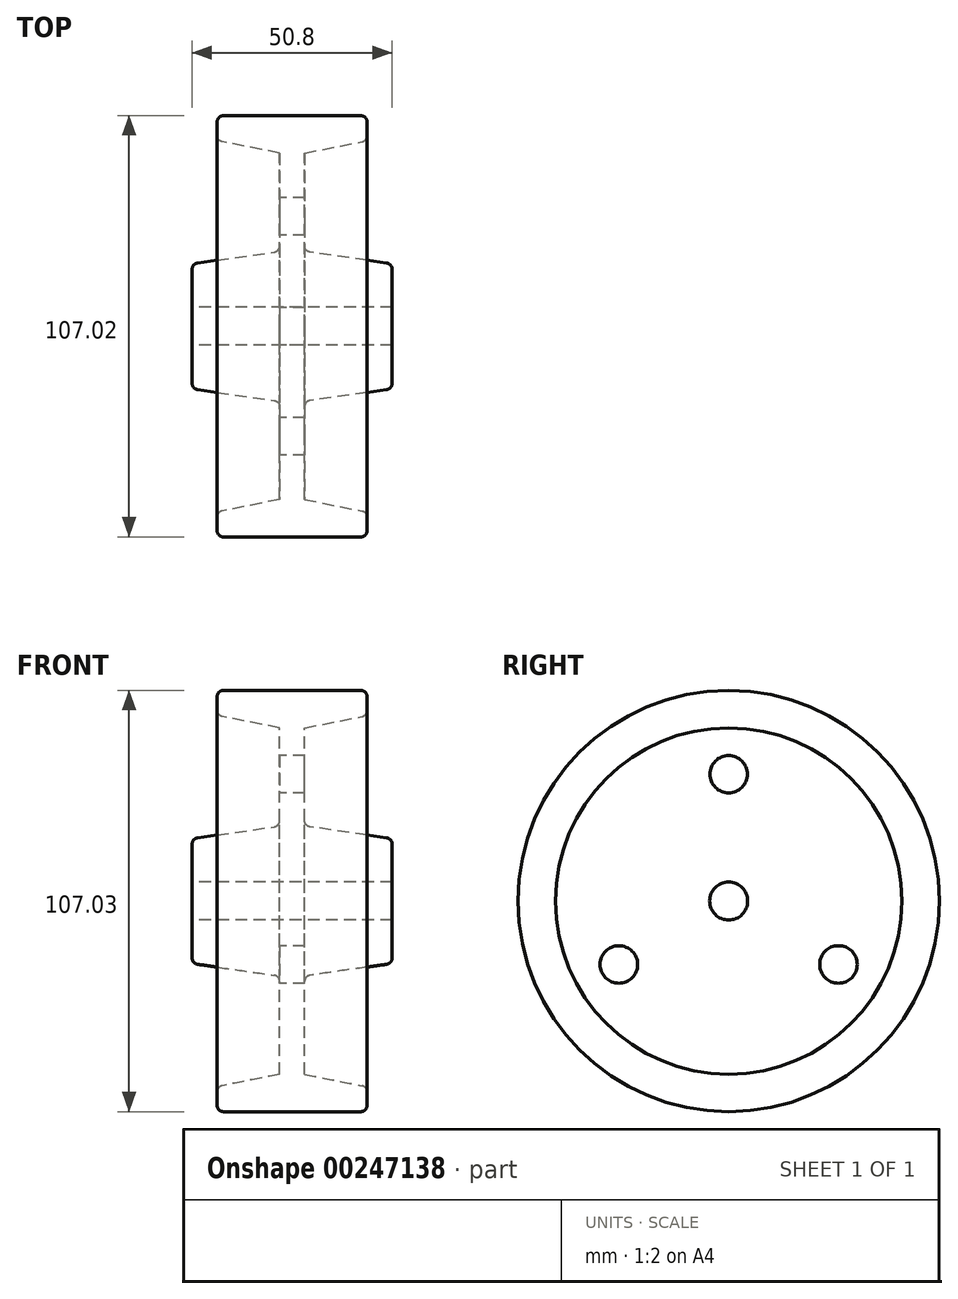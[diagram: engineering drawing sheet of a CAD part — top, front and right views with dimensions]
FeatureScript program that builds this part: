
annotation { "Feature Type Name" : "Feature", "Feature Type Description" : "" }
export const myFeature = defineFeature(function(context is Context, id is Id, definition is map)
    precondition{}
    {
        {
            var Q0;
            Q0=qCreatedBy(makeId("Front.planeOp"),FACE);
            var sketch = newSketch(context, id + "F0", { "sketchPlane" : qUnion([Q0])});
            skLineSegment(sketch, "E0", {"start": v(-20.15, 37.64) * mm, "end": v(14.77, 37.64) * mm});
            skLineSegment(sketch, "E1", {"start": v(-21.74, 36.05) * mm, "end": v(-21.74, 32.59) * mm});
            skLineSegment(sketch, "E2", {"start": v(16.36, 36.05) * mm, "end": v(16.36, 32.59) * mm});
            skLineSegment(sketch, "E3", {"start": v(0.48, 28.11) * mm, "end": v(-5.87, 28.11) * mm});
            skLineSegment(sketch, "E4", {"start": v(-2.7, 20.18) * mm, "end": v(-5.87, 20.18) * mm});
            skPoint(sketch, "E4.startSnap0", {"position": v(-2.7, 37.64) * mm});
            skLineSegment(sketch, "E5", {"start": v(-2.7, 20.18) * mm, "end": v(0.48, 20.18) * mm});
            skLineSegment(sketch, "E6", {"start": v(-5.87, 20.18) * mm, "end": v(-5.87, 28.11) * mm});
            skLineSegment(sketch, "E7", {"start": v(0.48, 20.18) * mm, "end": v(0.48, 28.11) * mm});
            skLineSegment(sketch, "E8", {"start": v(-20.47, 31.03) * mm, "end": v(-5.87, 28.11) * mm});
            skLineSegment(sketch, "E9", {"start": v(15.08, 31.03) * mm, "end": v(0.48, 28.11) * mm});
            skLineSegment(sketch, "E10", {"start": v(-5.87, 20.18) * mm, "end": v(-5.87, 10.65) * mm});
            skLineSegment(sketch, "E11", {"start": v(0.48, 20.18) * mm, "end": v(0.48, 10.65) * mm});
            skPoint(sketch, "E12.start.orphan", {"position": v(22.04, 37.64) * mm});
            skLineSegment(sketch, "E13", {"start": v(-5.87, 10.65) * mm, "end": v(0.48, 10.65) * mm});
            skPoint(sketch, "E14.visualSharp", {"position": v(-21.74, 37.64) * mm});
            skArc(sketch, "E14.filletArc", {"start": v(-20.15, 37.64) * mm, "mid": v(-21.28, 37.17) * mm, "end": v(-21.74, 36.05) * mm});
            skPoint(sketch, "E15.visualSharp", {"position": v(16.36, 37.64) * mm});
            skArc(sketch, "E15.filletArc", {"start": v(16.36, 36.05) * mm, "mid": v(15.9, 37.17) * mm, "end": v(14.77, 37.64) * mm});
            skPoint(sketch, "E16.visualSharp", {"position": v(16.36, 31.29) * mm});
            skArc(sketch, "E16.filletArc", {"start": v(15.08, 31.03) * mm, "mid": v(16, 31.58) * mm, "end": v(16.36, 32.59) * mm});
            skPoint(sketch, "E17.visualSharp", {"position": v(-21.74, 31.29) * mm});
            skArc(sketch, "E17.filletArc", {"start": v(-21.74, 32.59) * mm, "mid": v(-21.38, 31.58) * mm, "end": v(-20.47, 31.03) * mm});
            skPoint(sketch, "E18.visualSharp", {"position": v(0.48, 3.18) * mm});
            skPoint(sketch, "E19.visualSharp", {"position": v(-5.87, 3.17) * mm});
            skLineSegment(sketch, "E20", {"start": v(-5.87, 10.65) * mm, "end": v(-5.87, 4.55) * mm});
            skLineSegment(sketch, "E21", {"start": v(0.48, 10.65) * mm, "end": v(0.48, 4.55) * mm});
            skLineSegment(sketch, "E22", {"start": v(-7.23, 2.98) * mm, "end": v(-26.73, 0.2) * mm});
            skLineSegment(sketch, "E23", {"start": v(1.85, 2.98) * mm, "end": v(21.35, 0.2) * mm});
            skLineSegment(sketch, "E24", {"start": v(22.7, -1.38) * mm, "end": v(22.7, -14.29) * mm});
            skLineSegment(sketch, "E25", {"start": v(-28.1, -1.38) * mm, "end": v(-28.1, -14.29) * mm});
            skLineSegment(sketch, "E26", {"start": v(21.12, -15.88) * mm, "end": v(-26.5, -15.88) * mm});
            skArc(sketch, "E27.filletArc", {"start": v(0.48, 4.55) * mm, "mid": v(0.87, 3.51) * mm, "end": v(1.85, 2.98) * mm});
            skArc(sketch, "E28.filletArc", {"start": v(-7.23, 2.98) * mm, "mid": v(-6.25, 3.51) * mm, "end": v(-5.87, 4.55) * mm});
            skPoint(sketch, "E29.visualSharp", {"position": v(22.7, 0) * mm});
            skArc(sketch, "E29.filletArc", {"start": v(22.7, -1.38) * mm, "mid": v(22.32, -0.34) * mm, "end": v(21.35, 0.2) * mm});
            skPoint(sketch, "E30.visualSharp", {"position": v(22.7, -15.88) * mm});
            skArc(sketch, "E30.filletArc", {"start": v(21.12, -15.88) * mm, "mid": v(22.24, -15.41) * mm, "end": v(22.7, -14.29) * mm});
            skPoint(sketch, "E31.visualSharp", {"position": v(-28.1, -15.88) * mm});
            skArc(sketch, "E31.filletArc", {"start": v(-28.1, -14.29) * mm, "mid": v(-27.63, -15.41) * mm, "end": v(-26.5, -15.88) * mm});
            skPoint(sketch, "E32.visualSharp", {"position": v(-28.1, 0) * mm});
            skArc(sketch, "E32.filletArc", {"start": v(-26.73, 0.2) * mm, "mid": v(-27.7, -0.34) * mm, "end": v(-28.1, -1.38) * mm});
            skSolve(sketch);
        }
        {
            var Q0;
            Q0=makeQuery(id+"F0.imprint","IMPRINT",FACE,{"disambiguationData":[TD([[makeQuery(id+"F0.imprint","IMPRINT",EDGE,{"derivedFrom":sQuery(id+"F0.wireOp",EDGE,"E3")}),1.0]])]});
            var Q1;
            Q1=makeQuery(id+"F0.imprint","IMPRINT",FACE,{"disambiguationData":[TD([[makeQuery(id+"F0.imprint","IMPRINT",EDGE,{"derivedFrom":sQuery(id+"F0.wireOp",EDGE,"E13")}),-1.0]])]});
            var Q2;
            Q2=makeQuery(id+"F0.imprint","IMPRINT",FACE,{"disambiguationData":[TD([[makeQuery(id+"F0.imprint","IMPRINT",EDGE,{"derivedFrom":sQuery(id+"F0.wireOp",EDGE,"E4")}),1.0]])]});
            var Q3;
            Q3=makeQuery(id+"F0.imprint","IMPRINT",FACE,{"disambiguationData":[TD([[makeQuery(id+"F0.imprint","IMPRINT",EDGE,{"derivedFrom":sQuery(id+"F0.wireOp",EDGE,"E0")}),-1.0]])]});
            var Q4;
            Q4=sQuery(id+"F0.wireOp",EDGE,"E26");
            revolve(context, id + "F1", {"entities" : qUnion([Q0, Q1, Q2, Q3]), "axis" : qUnion([Q4]), "revolveType" : RevolveType.FULL});
        }
        {
            var Q0;
            Q0=makeQuery(id+"F1.opRevolve","SWEPT_FACE",FACE,{"disambiguationData":[OSD([sQuery(id+"F0.wireOp",EDGE,"E25")])]});
            var sketch = newSketch(context, id + "F2", { "sketchPlane" : qUnion([Q0])});
            skCircle(sketch, "E33", {"center": v(0, -15.88) * mm, "radius": 4.83 * mm});
            skSolve(sketch);
        }
        {
            var Q0;
            Q0=makeQuery(id+"F2.imprint","IMPRINT",FACE,{"disambiguationData":[TD([[makeQuery(id+"F2.imprint","IMPRINT",EDGE,{"derivedFrom":sQuery(id+"F2.wireOp",EDGE,"E33")}),1.0]])]});
            var Q1;
            Q1=makeQuery(id+"F2.imprint","IMPRINT",FACE,{"disambiguationData":[TD([[makeQuery(id+"F2.imprint","IMPRINT",EDGE,{"derivedFrom":makeQuery(id+"F1.opRevolve","SWEPT_EDGE",EDGE,{"disambiguationData":[OSD([sQuery(id+"F0.wireOp",EDGE,"E25"),sQuery(id+"F0.wireOp",EDGE,"E31.filletArc")])]})}),-1.0]])]});
            extrude(context, id + "F3", {"entities" : qUnion([Q0, Q1]), "operationType" : NewBodyOperationType.REMOVE, "endBound" : BoundingType.THROUGH_ALL, "oppositeDirection" : true, "depth" : 25.4 * mm});
        }
        {
            var Q0;
            Q0=makeQuery(id+"F1.opRevolve","SWEPT_FACE",FACE,{"disambiguationData":[OSD([sQuery(id+"F0.wireOp",EDGE,"E6"),sQuery(id+"F0.wireOp",EDGE,"E10"),sQuery(id+"F0.wireOp",EDGE,"E20")])]});
            var sketch = newSketch(context, id + "F4", { "sketchPlane" : qUnion([Q0])});
            skLineSegment(sketch, "E34", {"start": v(0, 11.58) * mm, "end": v(0, 16.35) * mm});
            skCircle(sketch, "E35", {"center": v(0, 16.35) * mm, "radius": 4.76 * mm});
            skCircle(sketch, "E36", {"center": v(27.9, -31.98) * mm, "radius": 4.76 * mm});
            skCircle(sketch, "E37", {"center": v(-27.89, -31.98) * mm, "radius": 4.76 * mm});
            skPoint(sketch, "E38.orphan", {"position": v(0, -15.88) * mm});
            skSolve(sketch);
        }
        {
            var Q0;
            Q0 = qSketchRegion(id + "F4", true);
            extrude(context, id + "F5", {"entities" : qUnion([Q0]), "operationType" : NewBodyOperationType.REMOVE, "endBound" : BoundingType.THROUGH_ALL, "oppositeDirection" : true, "depth" : 25.4 * mm});
        }
    });
